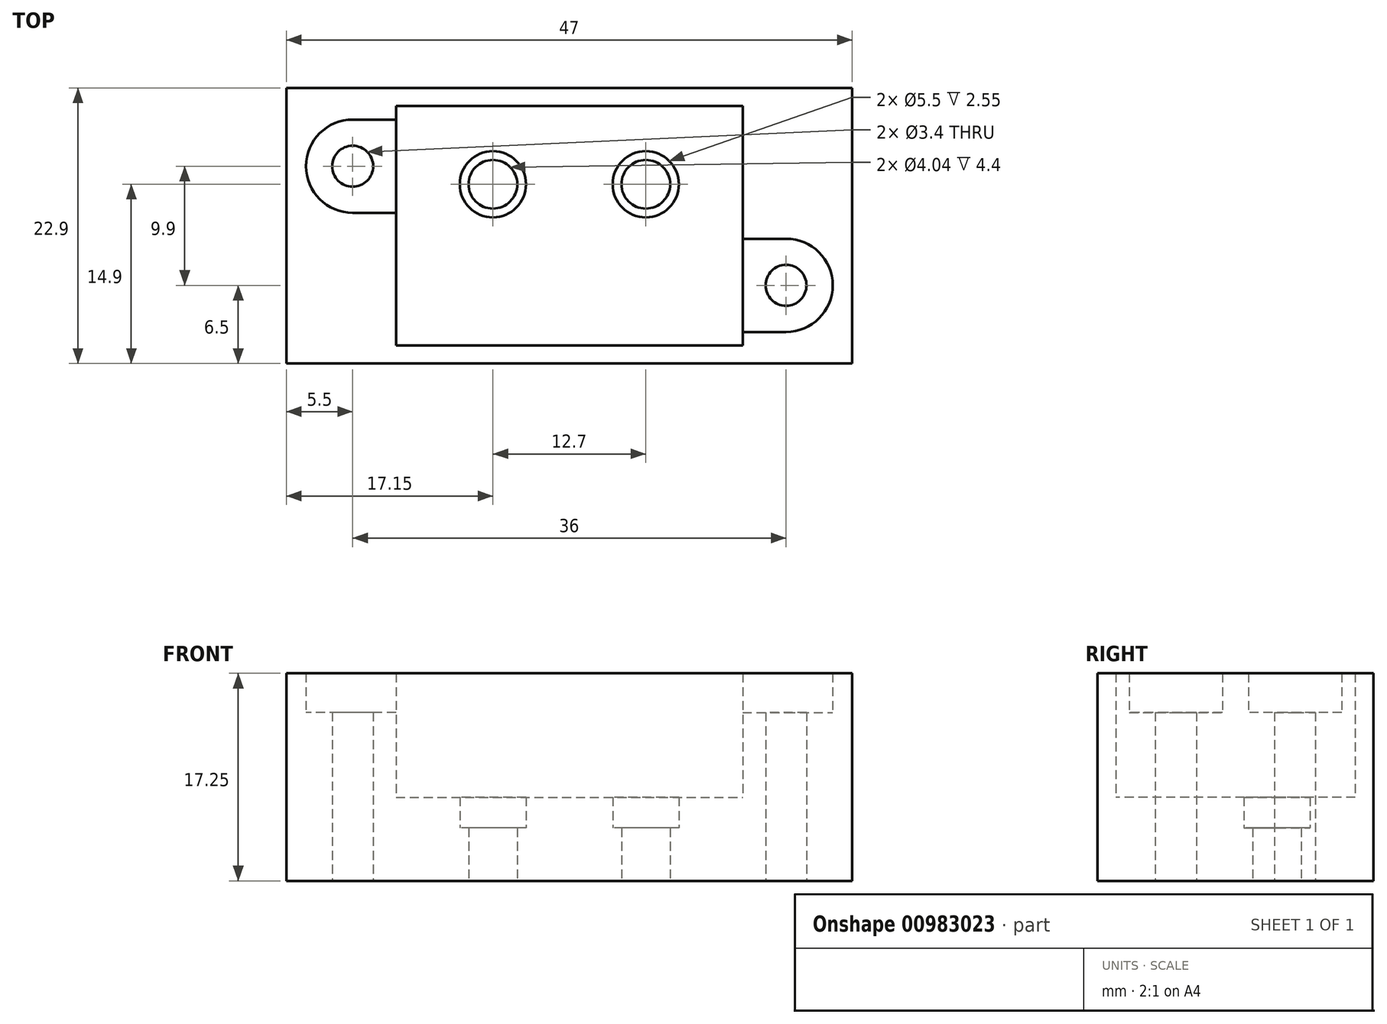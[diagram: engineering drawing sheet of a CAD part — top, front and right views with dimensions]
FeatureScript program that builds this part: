
annotation { "Feature Type Name" : "Feature", "Feature Type Description" : "" }
export const myFeature = defineFeature(function(context is Context, id is Id, definition is map)
    precondition{}
    {
        {
            var Q0;
            Q0=qCreatedBy(makeId("Top.planeOp"),FACE);
            var sketch = newSketch(context, id + "F0", { "sketchPlane" : qUnion([Q0])});
            skLineSegment(sketch, "E0.bottom", {"start": v(-23.5, 11.45) * mm, "end": v(23.5, 11.45) * mm});
            skLineSegment(sketch, "E0.top", {"start": v(-23.5, -11.45) * mm, "end": v(23.5, -11.45) * mm});
            skLineSegment(sketch, "E0.left", {"start": v(-23.5, 11.45) * mm, "end": v(-23.5, -11.45) * mm});
            skLineSegment(sketch, "E0.right", {"start": v(23.5, 11.45) * mm, "end": v(23.5, -11.45) * mm});
            skLineSegment(sketch, "E1.bottom", {"start": v(-14.4, 9.95) * mm, "end": v(14.4, 9.95) * mm});
            skLineSegment(sketch, "E1.top", {"start": v(-14.4, -9.95) * mm, "end": v(14.4, -9.95) * mm});
            skLineSegment(sketch, "E1.left", {"start": v(-14.4, 9.95) * mm, "end": v(-14.4, -9.95) * mm});
            skLineSegment(sketch, "E1.right", {"start": v(14.4, 9.95) * mm, "end": v(14.4, -9.95) * mm});
            skLineSegment(sketch, "E2", {"start": v(14.4, -1.07) * mm, "end": v(18, -1.07) * mm});
            skLineSegment(sketch, "E3", {"start": v(14.4, -8.82) * mm, "end": v(18, -8.82) * mm});
            skLineSegment(sketch, "E4", {"start": v(-14.4, 8.83) * mm, "end": v(-18, 8.83) * mm});
            skLineSegment(sketch, "E5", {"start": v(-14.4, 1.08) * mm, "end": v(-18, 1.08) * mm});
            skArc(sketch, "E6", {"start": v(-18, 8.83) * mm, "mid": v(-21.88, 4.95) * mm, "end": v(-18, 1.08) * mm});
            skArc(sketch, "E7", {"start": v(18, -8.82) * mm, "mid": v(21.88, -4.95) * mm, "end": v(18, -1.07) * mm});
            skCircle(sketch, "E8", {"center": v(18, -4.95) * mm, "radius": 1.7 * mm});
            skCircle(sketch, "E9", {"center": v(-18, 4.95) * mm, "radius": 1.7 * mm});
            skCircle(sketch, "E10", {"center": v(-6.35, 3.45) * mm, "radius": 2.02 * mm});
            skCircle(sketch, "E11", {"center": v(6.35, 3.45) * mm, "radius": 2.02 * mm});
            skCircle(sketch, "E12", {"center": v(6.35, 3.45) * mm, "radius": 2.75 * mm});
            skCircle(sketch, "E13", {"center": v(-6.35, 3.45) * mm, "radius": 2.75 * mm});
            skSolve(sketch);
        }
        {
            var Q0;
            Q0=makeQuery(id+"F0.imprint","IMPRINT",FACE,{"disambiguationData":[TD([[makeQuery(id+"F0.imprint","IMPRINT",EDGE,{"derivedFrom":sQuery(id+"F0.wireOp",EDGE,"E0.bottom")}),-1.0]])]});
            extrude(context, id + "F1", {"entities" : qUnion([Q0]), "depth" : 17.25 * mm, "offsetDistance" : 25 * mm});
        }
        {
            var Q0;
            {var subQ3=sQuery(id+"F0.wireOp",EDGE,"E1.bottom");Q0=makeQuery(id+"F0.imprint","IMPRINT",FACE,{"disambiguationData":[TD([[makeQuery(id+"F0.imprint","IMPRINT",EDGE,{"derivedFrom":subQ3}),-1.0]])]});}
            extrude(context, id + "F2", {"entities" : qUnion([Q0]), "operationType" : NewBodyOperationType.ADD, "depth" : 6.95 * mm, "offsetDistance" : 25 * mm});
        }
        {
            var Q0;
            {var subQ1=sQuery(id+"F0.wireOp",EDGE,"E2");Q0=makeQuery(id+"F0.imprint","IMPRINT",FACE,{"disambiguationData":[TD([[makeQuery(id+"F0.imprint","IMPRINT",EDGE,{"derivedFrom":subQ1}),-1.0]])]});}
            var Q1;
            {var subQ1=sQuery(id+"F0.wireOp",EDGE,"E4");Q1=makeQuery(id+"F0.imprint","IMPRINT",FACE,{"disambiguationData":[TD([[makeQuery(id+"F0.imprint","IMPRINT",EDGE,{"derivedFrom":subQ1}),1.0]])]});}
            extrude(context, id + "F3", {"entities" : qUnion([Q0, Q1]), "operationType" : NewBodyOperationType.ADD, "depth" : 14 * mm, "offsetDistance" : 25 * mm});
        }
        {
            var Q0;
            Q0=makeQuery(id+"F0.imprint","IMPRINT",FACE,{"disambiguationData":[TD([[makeQuery(id+"F0.imprint","IMPRINT",EDGE,{"derivedFrom":sQuery(id+"F0.wireOp",EDGE,"E10")}),-1.0]])]});
            var Q1;
            Q1=makeQuery(id+"F0.imprint","IMPRINT",FACE,{"disambiguationData":[TD([[makeQuery(id+"F0.imprint","IMPRINT",EDGE,{"derivedFrom":sQuery(id+"F0.wireOp",EDGE,"E11")}),-1.0]])]});
            extrude(context, id + "F4", {"entities" : qUnion([Q0, Q1]), "operationType" : NewBodyOperationType.ADD, "depth" : 4.4 * mm, "offsetDistance" : 25 * mm});
        }
    });
